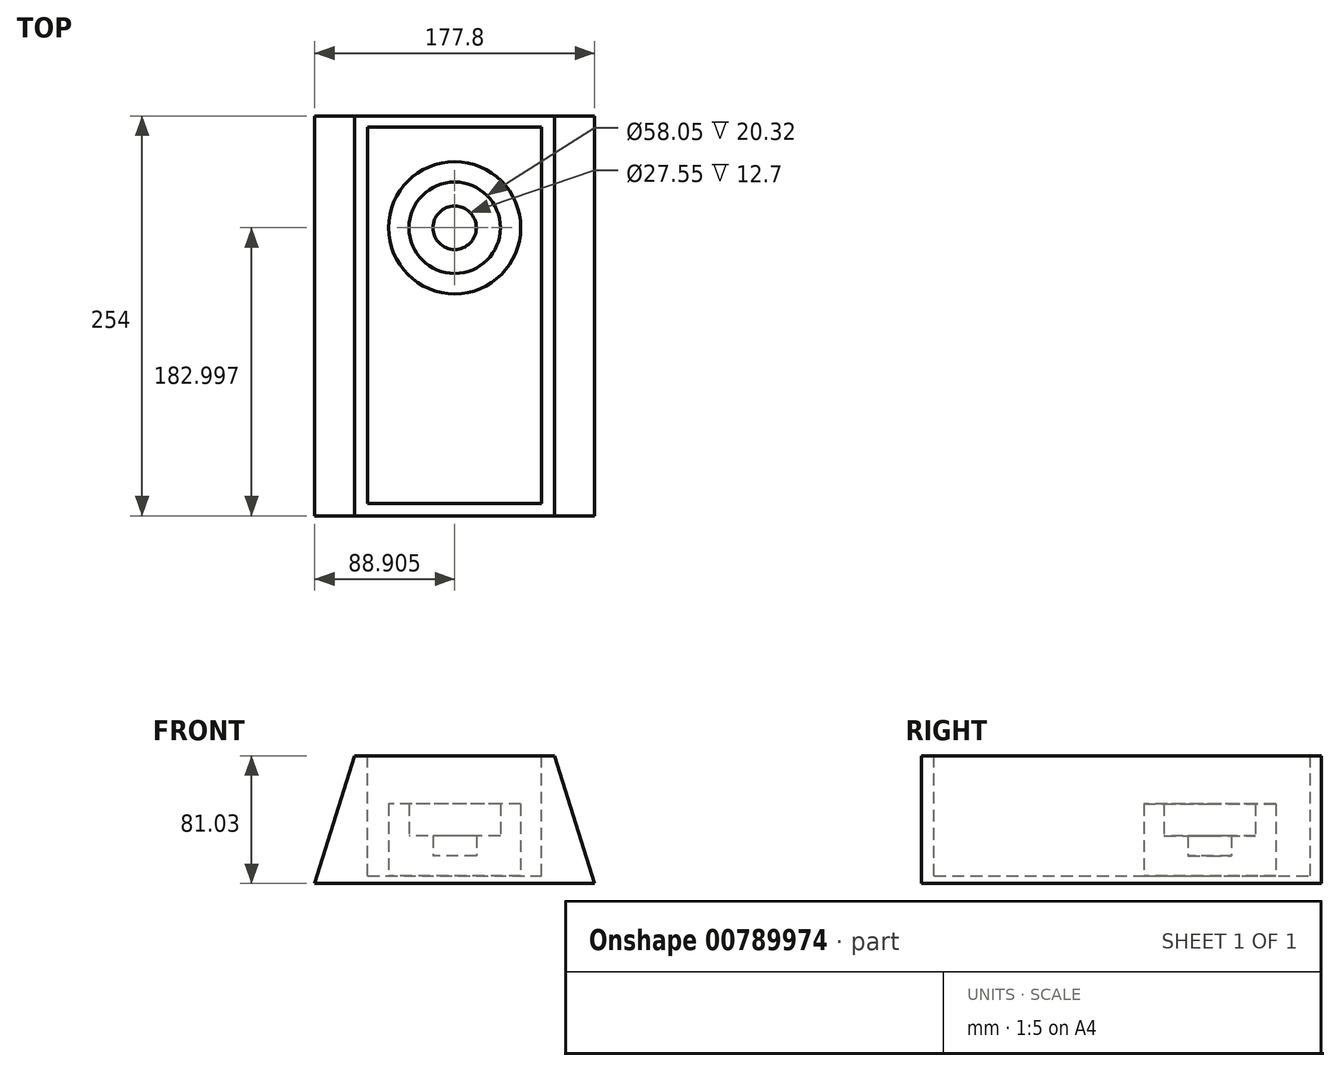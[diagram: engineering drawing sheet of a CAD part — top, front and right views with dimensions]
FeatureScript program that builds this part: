
annotation { "Feature Type Name" : "Feature", "Feature Type Description" : "" }
export const myFeature = defineFeature(function(context is Context, id is Id, definition is map)
    precondition{}
    {
        {
            var Q0;
            Q0=qCreatedBy(makeId("Front.planeOp"),FACE);
            var sketch = newSketch(context, id + "F0", { "sketchPlane" : qUnion([Q0])});
            skLineSegment(sketch, "E0", {"start": v(-71.97, 0) * mm, "end": v(55.03, 0) * mm});
            skLineSegment(sketch, "E1", {"start": v(55.03, 0) * mm, "end": v(80.43, -81.03) * mm});
            skLineSegment(sketch, "E2", {"start": v(80.43, -81.03) * mm, "end": v(-97.37, -81.03) * mm});
            skLineSegment(sketch, "E3", {"start": v(-97.37, -81.03) * mm, "end": v(-71.97, 0) * mm});
            skSolve(sketch);
        }
        {
            var Q0;
            Q0=makeQuery(id+"F0.imprint","IMPRINT",FACE,{"disambiguationData":[TD([[makeQuery(id+"F0.imprint","IMPRINT",EDGE,{"derivedFrom":sQuery(id+"F0.wireOp",EDGE,"E0")}),-1.0]])]});
            extrude(context, id + "F1", {"entities" : qUnion([Q0]), "depth" : 254 * mm, "offsetDistance" : 25.4 * mm});
        }
        {
            var Q0;
            Q0=makeQuery(id+"F1.opExtrude","SWEPT_FACE",FACE,{"disambiguationData":[OSD([sQuery(id+"F0.wireOp",EDGE,"E0")])]});
            var sketch = newSketch(context, id + "F2", { "sketchPlane" : qUnion([Q0])});
            skLineSegment(sketch, "E4.bottom", {"start": v(-63.72, -246.03) * mm, "end": v(46.8, -246.03) * mm});
            skLineSegment(sketch, "E4.top", {"start": v(-63.72, -7.16) * mm, "end": v(46.8, -7.16) * mm});
            skLineSegment(sketch, "E4.left", {"start": v(-63.72, -246.03) * mm, "end": v(-63.72, -7.16) * mm});
            skLineSegment(sketch, "E4.right", {"start": v(46.8, -246.03) * mm, "end": v(46.8, -7.16) * mm});
            skSolve(sketch);
        }
        {
            var Q0;
            Q0 = qSketchRegion(id + "F2", true);
            extrude(context, id + "F3", {"entities" : qUnion([Q0]), "operationType" : NewBodyOperationType.REMOVE, "oppositeDirection" : true, "depth" : 76.2 * mm, "offsetDistance" : 25.4 * mm});
        }
        {
            var Q0;
            Q0=makeQuery(id+"F3.boolean.opBoolean","COPY",FACE,{"derivedFrom":makeQuery(id+"F3.opExtrude","CAP_FACE",FACE,{"disambiguationData":[OSD([sQuery(id+"F2.wireOp",EDGE,"E4.bottom"),sQuery(id+"F2.wireOp",EDGE,"E4.top"),sQuery(id+"F2.wireOp",EDGE,"E4.left"),sQuery(id+"F2.wireOp",EDGE,"E4.right")])],"isStart":false})});
            var sketch = newSketch(context, id + "F4", { "sketchPlane" : qUnion([Q0])});
            skCircle(sketch, "E5", {"center": v(-8.46, -71) * mm, "radius": 13.78 * mm});
            skPoint(sketch, "E5.centerSnap0", {"position": v(-8.46, -7.16) * mm});
            skCircle(sketch, "E6", {"center": v(-8.46, -71) * mm, "radius": 29.02 * mm});
            skCircle(sketch, "E7", {"center": v(-8.46, -71) * mm, "radius": 41.97 * mm});
            skLineSegment(sketch, "E8", {"start": v(-17.38, -246.03) * mm, "end": v(-17.38, -112.01) * mm});
            skLineSegment(sketch, "E9", {"start": v(0, -246.03) * mm, "end": v(0, -112.11) * mm});
            skPoint(sketch, "E9.startSnap0", {"position": v(-8.46, -246.03) * mm});
            skSolve(sketch);
        }
        {
            var Q0;
            Q0=makeQuery(id+"F4.imprint","IMPRINT",FACE,{"disambiguationData":[TD([[makeQuery(id+"F4.imprint","IMPRINT",EDGE,{"derivedFrom":sQuery(id+"F4.wireOp",EDGE,"E5")}),1.0]])]});
            extrude(context, id + "F5", {"entities" : qUnion([Q0]), "operationType" : NewBodyOperationType.ADD, "depth" : 12.7 * mm, "offsetDistance" : 25.4 * mm});
        }
        {
            var Q0;
            Q0=makeQuery(id+"F4.imprint","IMPRINT",FACE,{"disambiguationData":[TD([[makeQuery(id+"F4.imprint","IMPRINT",EDGE,{"derivedFrom":sQuery(id+"F4.wireOp",EDGE,"E5")}),-1.0]])]});
            extrude(context, id + "F6", {"entities" : qUnion([Q0]), "operationType" : NewBodyOperationType.ADD, "depth" : 25.4 * mm, "offsetDistance" : 25.4 * mm});
        }
        {
            var Q0;
            Q0=makeQuery(id+"F4.imprint","IMPRINT",FACE,{"disambiguationData":[TD([[makeQuery(id+"F4.imprint","IMPRINT",EDGE,{"derivedFrom":sQuery(id+"F4.wireOp",EDGE,"E6")}),-1.0]])]});
            extrude(context, id + "F7", {"entities" : qUnion([Q0]), "operationType" : NewBodyOperationType.ADD, "depth" : 45.72 * mm, "offsetDistance" : 25.4 * mm});
        }
    });
